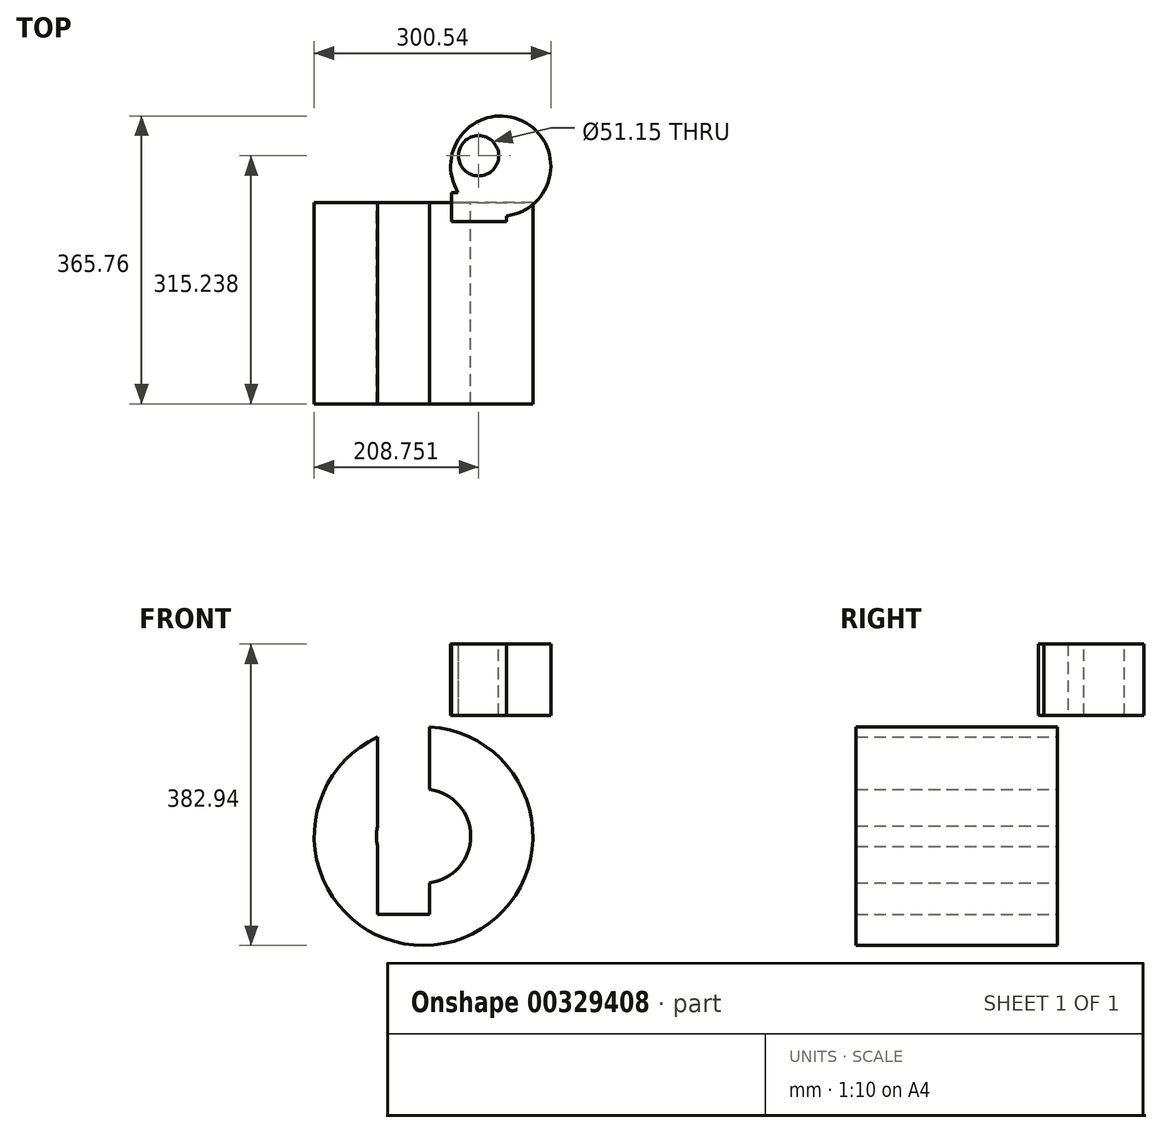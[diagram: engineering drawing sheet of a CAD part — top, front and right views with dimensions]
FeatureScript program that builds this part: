
annotation { "Feature Type Name" : "Feature", "Feature Type Description" : "" }
export const myFeature = defineFeature(function(context is Context, id is Id, definition is map)
    precondition{}
    {
        {
            var Q0;
            Q0=qCreatedBy(makeId("Top.planeOp"),FACE);
            var sketch = newSketch(context, id + "F0", { "sketchPlane" : qUnion([Q0])});
            skLineSegment(sketch, "E0.bottom", {"start": v(-38.23, 12.8) * mm, "end": v(31.14, 12.8) * mm});
            skLineSegment(sketch, "E0.top", {"start": v(-38.23, -24.51) * mm, "end": v(31.14, -24.51) * mm});
            skLineSegment(sketch, "E0.left", {"start": v(-38.23, 12.8) * mm, "end": v(-38.23, -24.51) * mm});
            skLineSegment(sketch, "E0.right", {"start": v(31.14, 12.8) * mm, "end": v(31.14, -24.51) * mm});
            skCircle(sketch, "E1", {"center": v(24.05, 46.1) * mm, "radius": 63.64 * mm});
            skSolve(sketch);
        }
        {
            var Q0;
            Q0 = qSketchRegion(id + "F0", true);
            extrude(context, id + "F1", {"entities" : qUnion([Q0]), "depth" : 90.68 * mm});
        }
        {
            var Q0;
            Q0=makeQuery(id+"F1.opExtrude","CAP_FACE",FACE,{"disambiguationData":[OSD([sQuery(id+"F0.wireOp",EDGE,"E0.bottom"),sQuery(id+"F0.wireOp",EDGE,"E0.top"),sQuery(id+"F0.wireOp",EDGE,"E0.left"),sQuery(id+"F0.wireOp",EDGE,"E0.right"),sQuery(id+"F0.wireOp",EDGE,"E1")])],"isStart":false});
            var sketch = newSketch(context, id + "F2", { "sketchPlane" : qUnion([Q0])});
            skCircle(sketch, "E2", {"center": v(-4.1, 59.2) * mm, "radius": 25.58 * mm});
            skSolve(sketch);
        }
        {
            var Q0;
            Q0=makeQuery(id+"F2.imprint","IMPRINT",FACE,{"disambiguationData":[TD([[makeQuery(id+"F2.imprint","IMPRINT",EDGE,{"derivedFrom":sQuery(id+"F2.wireOp",EDGE,"E2")}),1.0]])]});
            extrude(context, id + "F3", {"entities" : qUnion([Q0]), "operationType" : NewBodyOperationType.REMOVE, "oppositeDirection" : true, "depth" : 141.73 * mm});
        }
        {
            var Q0;
            Q0=qCreatedBy(makeId("Front.planeOp"),FACE);
            var sketch = newSketch(context, id + "F4", { "sketchPlane" : qUnion([Q0])});
            skLineSegment(sketch, "E3.bottom", {"start": v(-66.07, 74.8) * mm, "end": v(-132.35, 74.8) * mm});
            skLineSegment(sketch, "E3.top", {"start": v(-66.07, -252.7) * mm, "end": v(-132.35, -252.7) * mm});
            skLineSegment(sketch, "E3.left", {"start": v(-66.07, 74.8) * mm, "end": v(-66.07, -252.7) * mm});
            skLineSegment(sketch, "E3.right", {"start": v(-132.35, 74.8) * mm, "end": v(-132.35, -252.7) * mm});
            skPoint(sketch, "E3.middle", {"position": v(-99.21, -88.94) * mm});
            skCircle(sketch, "E4", {"center": v(-74.02, -153.43) * mm, "radius": 138.84 * mm});
            skCircle(sketch, "E5", {"center": v(-74.02, -153.43) * mm, "radius": 59.8 * mm});
            skSolve(sketch);
        }
        {
            var Q0;
            {var subQ6=sQuery(id+"F4.wireOp",EDGE,"E3.top");Q0=makeQuery(id+"F4.imprint","IMPRINT",FACE,{"disambiguationData":[TD([[makeQuery(id+"F4.imprint","IMPRINT",EDGE,{"derivedFrom":subQ6}),1.0]])]});}
            extrude(context, id + "F5", {"entities" : qUnion([Q0]), "depth" : 256.03 * mm});
        }
        {
            var Q0;
            Q0=makeQuery(id+"F5.opExtrude","CAP_FACE",FACE,{"disambiguationData":[OSD([sQuery(id+"F4.wireOp",EDGE,"E3.top"),sQuery(id+"F4.wireOp",EDGE,"E3.left"),sQuery(id+"F4.wireOp",EDGE,"E3.right"),sQuery(id+"F4.wireOp",EDGE,"E4"),sQuery(id+"F4.wireOp",EDGE,"E5")])],"isStart":false});
            var sketch = newSketch(context, id + "F6", { "sketchPlane" : qUnion([Q0])});
            skArc(sketch, "E6", {"start": v(-151.95, -225.06) * mm, "mid": v(-23.3, -222.68) * mm, "end": v(18.6, -101.02) * mm});
            skSolve(sketch);
        }
        {
            var Q0;
            Q0=sQuery(id+"F6.wireOp",EDGE,"E6");
            extrude(context, id + "F7", {"bodyType" : ToolBodyType.SURFACE, "surfaceEntities" : qUnion([Q0]), "depth" : 1171.2 * mm});
        }
    });
